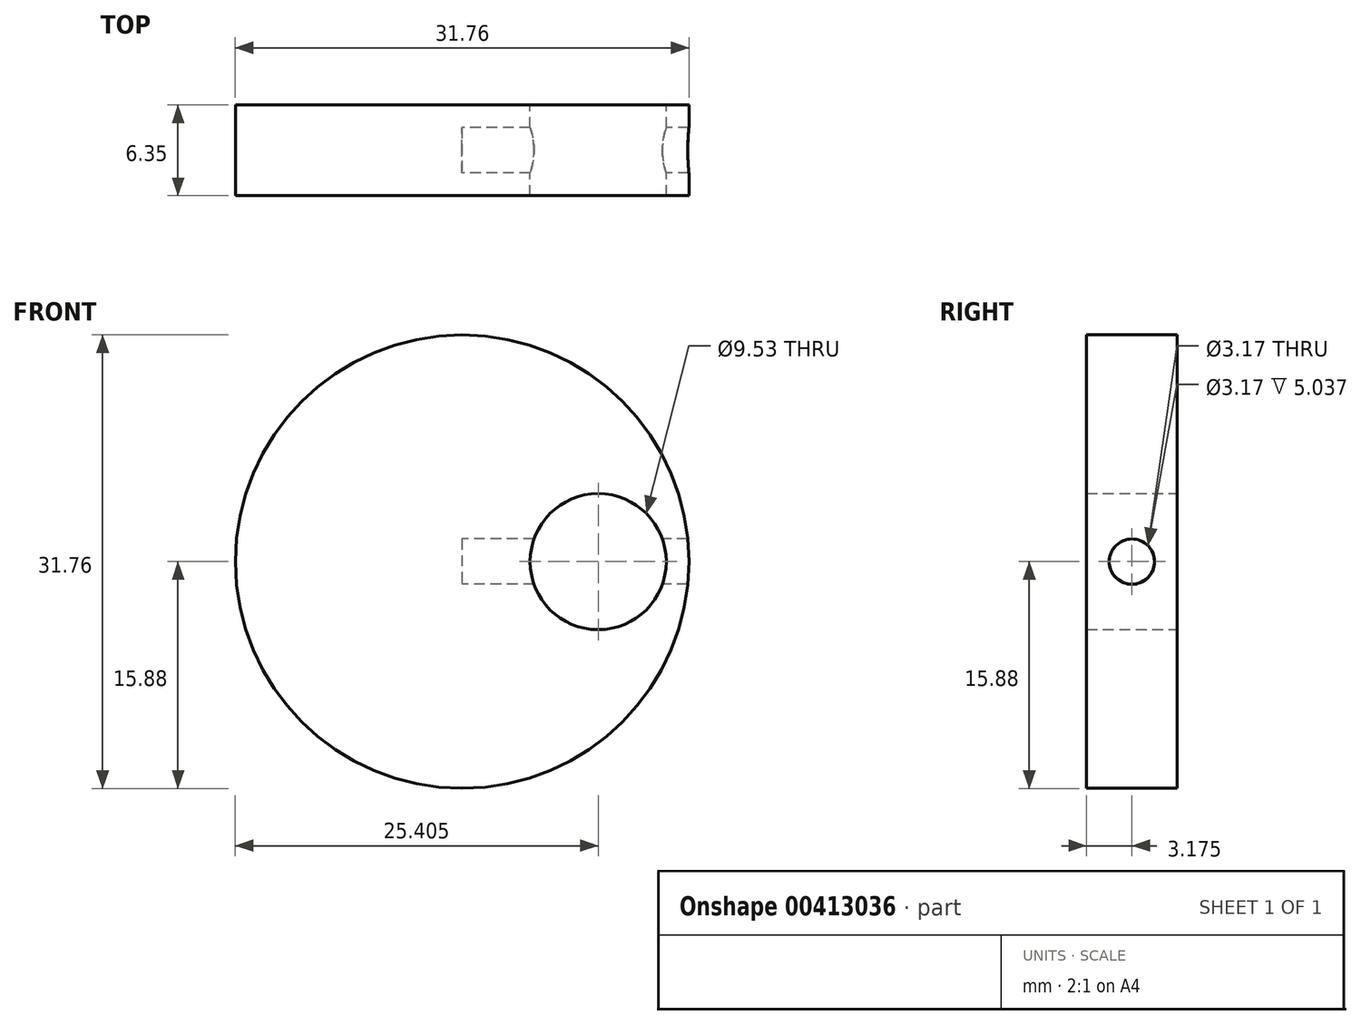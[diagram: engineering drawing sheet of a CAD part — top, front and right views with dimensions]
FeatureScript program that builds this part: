
annotation { "Feature Type Name" : "Feature", "Feature Type Description" : "" }
export const myFeature = defineFeature(function(context is Context, id is Id, definition is map)
    precondition{}
    {
        {
            var Q0;
            Q0=qCreatedBy(makeId("Front.planeOp"),FACE);
            var sketch = newSketch(context, id + "F0", { "sketchPlane" : qUnion([Q0])});
            skCircle(sketch, "E0", {"center": v(0, 0) * mm, "radius": 15.88 * mm});
            skCircle(sketch, "E1", {"center": v(9.53, 0) * mm, "radius": 4.76 * mm});
            skSolve(sketch);
        }
        {
            var Q0;
            Q0 = qSketchRegion(id + "F0", true);
            extrude(context, id + "F1", {"entities" : qUnion([Q0]), "depth" : 6.35 * mm});
        }
        {
            var Q0;
            Q0=qCreatedBy(makeId("Right.planeOp"),FACE);
            var sketch = newSketch(context, id + "F2", { "sketchPlane" : qUnion([Q0])});
            skPoint(sketch, "E2", {"position": v(-3.18, 0) * mm});
            skSolve(sketch);
        }
        {
            var Q0;
            Q0=sQuery(id+"F2.wireOp",VERTEX,"E2");
            var Q1;
            Q1=makeQuery(id+"F1.opExtrude","SWEPT_BODY",BODY,{"disambiguationData":[OSD([sQuery(id+"F0.wireOp",EDGE,"E0"),sQuery(id+"F0.wireOp",EDGE,"E1")])]});
            hole(context, id + "F3", {"style" : HoleStyle.C_BORE, "endStyle" : HoleEndStyle.THROUGH, "oppositeDirection" : true, "holeDiameter" : 3.17 * mm, "cBoreDiameter" : 3.17 * mm, "cBoreDepth" : 6.35 * mm, "isTappedThrough" : true, "tappedDepth" : 12.7 * mm, "tapClearance" : 3, "locations" : qUnion([Q0]), "scope" : qUnion([Q1])});
        }
    });
